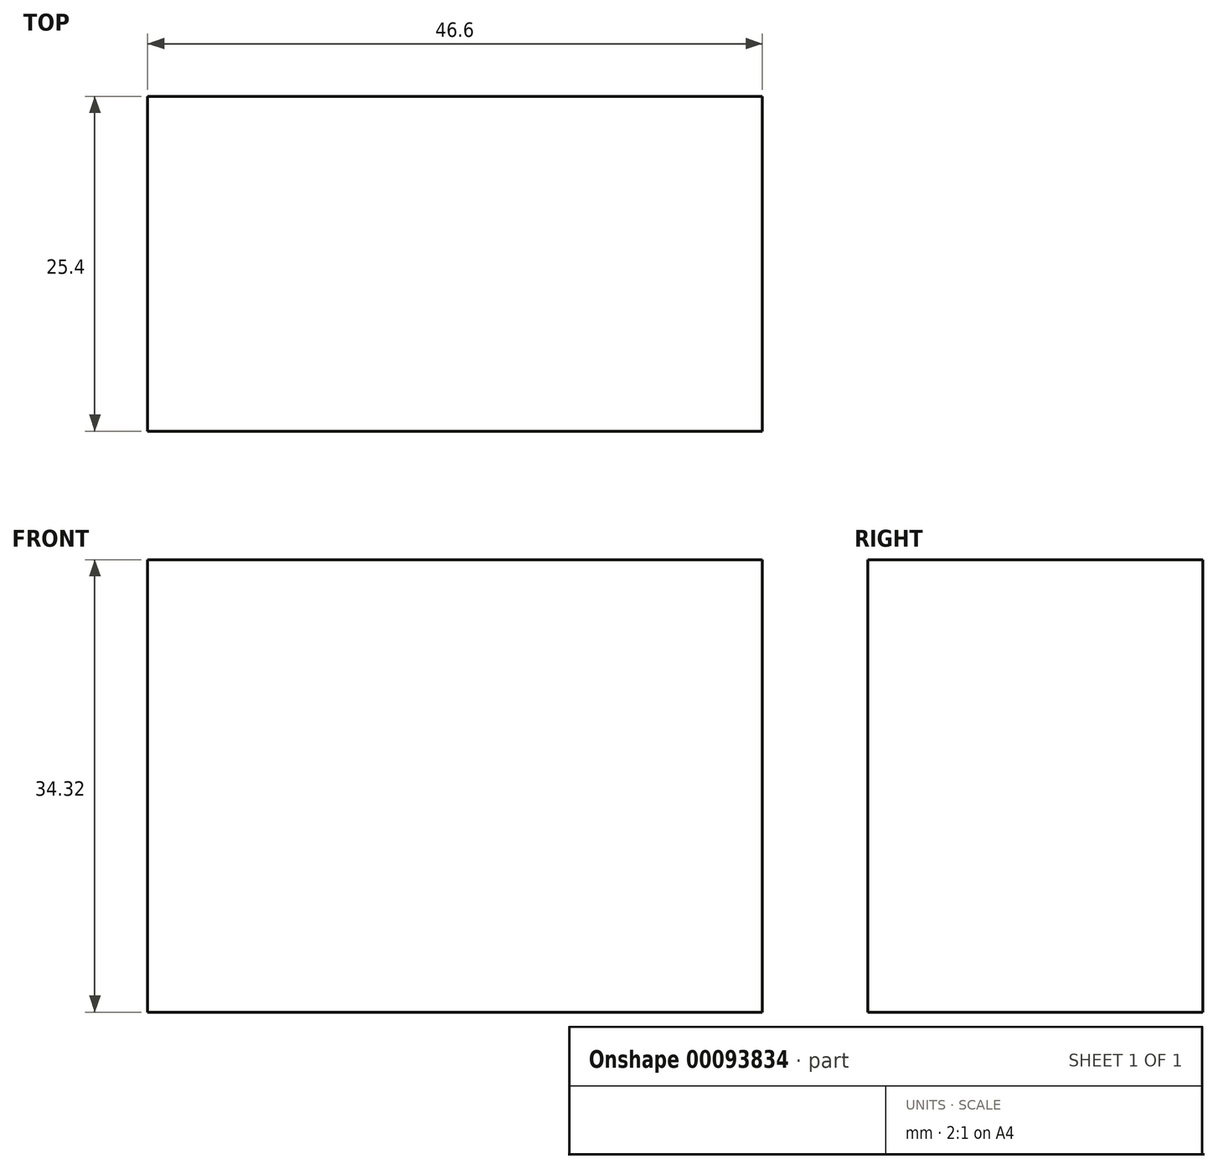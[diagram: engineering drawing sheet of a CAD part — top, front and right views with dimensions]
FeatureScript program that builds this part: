
annotation { "Feature Type Name" : "Feature", "Feature Type Description" : "" }
export const myFeature = defineFeature(function(context is Context, id is Id, definition is map)
    precondition{}
    {
        {
            var Q0;
            Q0=qCreatedBy(makeId("Front.planeOp"),FACE);
            var sketch = newSketch(context, id + "F0", { "sketchPlane" : qUnion([Q0])});
            skLineSegment(sketch, "E0.bottom", {"start": v(0, 0) * mm, "end": v(46.6, 0) * mm});
            skLineSegment(sketch, "E0.top", {"start": v(0, 34.32) * mm, "end": v(46.6, 34.32) * mm});
            skLineSegment(sketch, "E0.left", {"start": v(0, 0) * mm, "end": v(0, 34.32) * mm});
            skLineSegment(sketch, "E0.right", {"start": v(46.6, 0) * mm, "end": v(46.6, 34.32) * mm});
            skSolve(sketch);
        }
        {
            var Q0;
            Q0=makeQuery(id+"F0.imprint","IMPRINT",FACE,{"disambiguationData":[TD([[makeQuery(id+"F0.imprint","IMPRINT",EDGE,{"derivedFrom":sQuery(id+"F0.wireOp",EDGE,"E0.bottom")}),1.0]])]});
            extrude(context, id + "F1", {"entities" : qUnion([Q0]), "depth" : 25.4 * mm});
        }
    });
